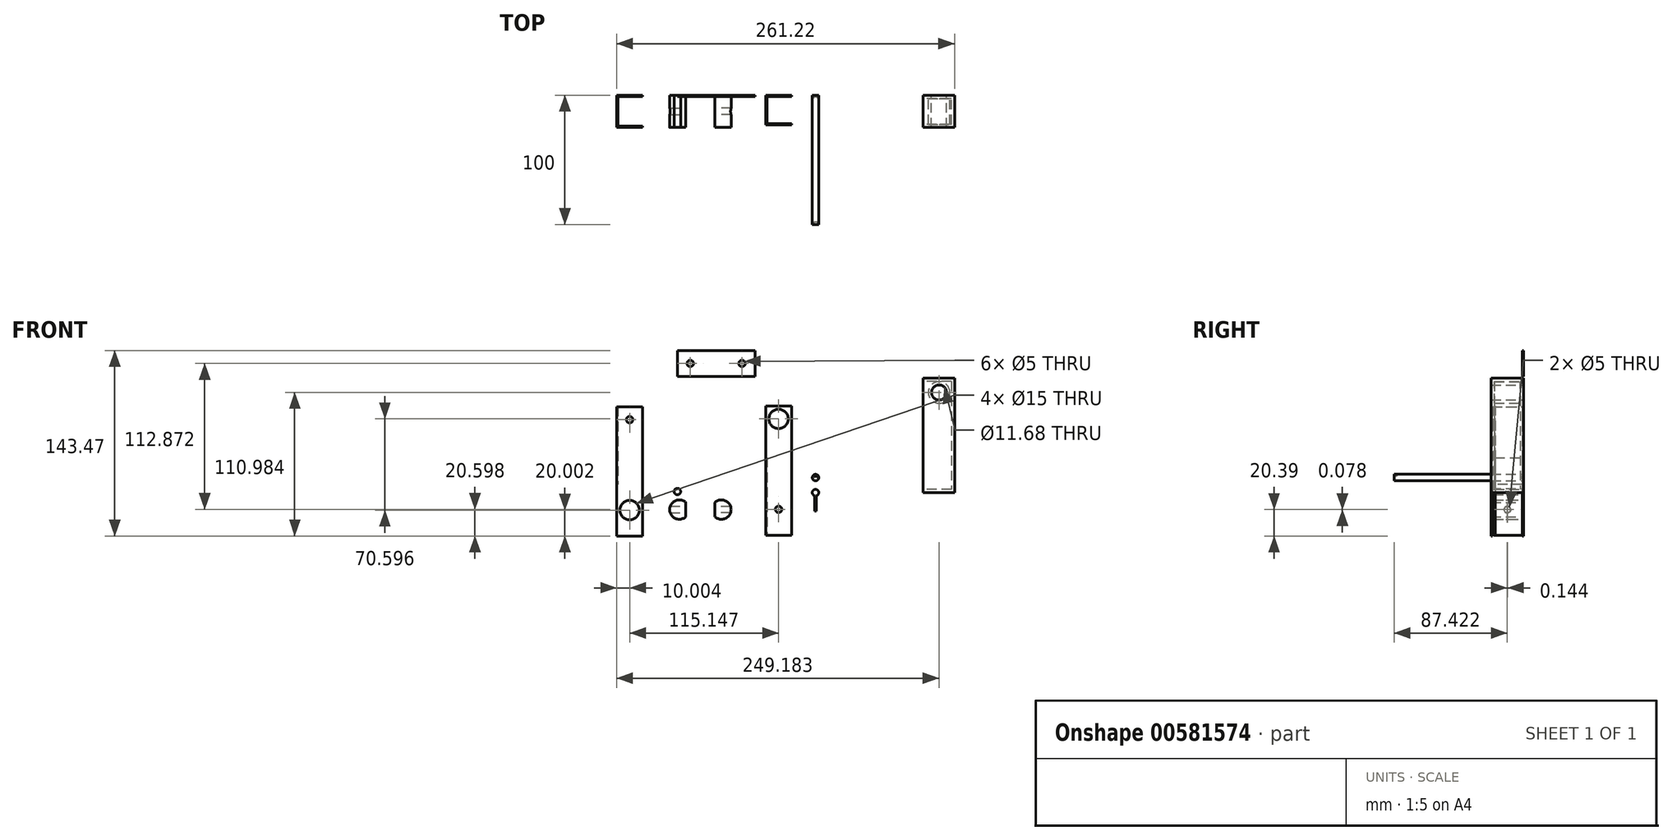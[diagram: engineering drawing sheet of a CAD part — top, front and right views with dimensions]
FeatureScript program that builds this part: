
annotation { "Feature Type Name" : "Feature", "Feature Type Description" : "" }
export const myFeature = defineFeature(function(context is Context, id is Id, definition is map)
    precondition{}
    {
        {
            var Q0;
            Q0=qCreatedBy(makeId("Front.planeOp"),FACE);
            var sketch = newSketch(context, id + "F0", { "sketchPlane" : qUnion([Q0])});
            skLineSegment(sketch, "E0.bottom", {"start": v(-95.37, 30.82) * mm, "end": v(-75.37, 30.82) * mm});
            skLineSegment(sketch, "E0.top", {"start": v(-95.37, -69.18) * mm, "end": v(-75.37, -69.18) * mm});
            skLineSegment(sketch, "E0.left", {"start": v(-95.37, 30.82) * mm, "end": v(-95.37, -69.18) * mm});
            skLineSegment(sketch, "E0.right", {"start": v(-75.37, 30.82) * mm, "end": v(-75.37, -69.18) * mm});
            skCircle(sketch, "E1", {"center": v(-85.37, 20.82) * mm, "radius": 2.5 * mm});
            skCircle(sketch, "E2", {"center": v(-85.37, -49.18) * mm, "radius": 7.5 * mm});
            skPoint(sketch, "E3.start.orphan", {"position": v(-85.37, 30.82) * mm});
            skCircle(sketch, "E4", {"center": v(-48.44, -34.8) * mm, "radius": 2.5 * mm});
            skArc(sketch, "E5", {"start": v(-41.92, -43.12) * mm, "mid": v(-54.42, -48.71) * mm, "end": v(-41.92, -54.3) * mm});
            skPoint(sketch, "E6.orphan", {"position": v(-95.37, 10.82) * mm});
            skPoint(sketch, "E7.start.orphan", {"position": v(-95.37, 20.82) * mm});
            skPoint(sketch, "E8.trimOffspring.end.orphan", {"position": v(-75.37, 20.82) * mm});
            skPoint(sketch, "E9.MirrorCS.end.orphan", {"position": v(-75.37, 10.82) * mm});
            skPoint(sketch, "E10.orphan", {"position": v(-95.37, 0.82) * mm});
            skPoint(sketch, "E11.MirrorCS.end.orphan", {"position": v(-75.37, 0.82) * mm});
            skPoint(sketch, "E12.orphan", {"position": v(-95.37, -19.18) * mm});
            skPoint(sketch, "E13.MirrorCS.end.orphan", {"position": v(-75.37, -19.18) * mm});
            skPoint(sketch, "E14.orphan", {"position": v(-95.37, -29.18) * mm});
            skPoint(sketch, "E15.MirrorCS.end.orphan", {"position": v(-75.37, -29.18) * mm});
            skPoint(sketch, "E16.orphan", {"position": v(-95.37, -59.18) * mm});
            skPoint(sketch, "E17.MirrorCS.end.orphan", {"position": v(-75.37, -59.18) * mm});
            skPoint(sketch, "E18.trimOffspring.end.orphan", {"position": v(-85.37, -69.18) * mm});
            skPoint(sketch, "E19.MirrorCS.start.orphan", {"position": v(-95.37, -49.18) * mm});
            skPoint(sketch, "E20.trimOffspring.end.orphan", {"position": v(-75.37, -49.18) * mm});
            skLineSegment(sketch, "E21.bottom", {"start": v(19.78, 31.42) * mm, "end": v(39.78, 31.42) * mm});
            skLineSegment(sketch, "E21.top", {"start": v(19.78, -68.58) * mm, "end": v(39.78, -68.58) * mm});
            skLineSegment(sketch, "E21.left", {"start": v(19.78, 31.42) * mm, "end": v(19.78, -68.58) * mm});
            skLineSegment(sketch, "E21.right", {"start": v(39.78, 31.42) * mm, "end": v(39.78, -68.58) * mm});
            skCircle(sketch, "E22", {"center": v(29.78, 21.42) * mm, "radius": 7.5 * mm});
            skCircle(sketch, "E23", {"center": v(29.78, -48.58) * mm, "radius": 2.5 * mm});
            skPoint(sketch, "E24.start.orphan", {"position": v(29.78, 31.42) * mm});
            skPoint(sketch, "E25.orphan", {"position": v(19.78, 11.42) * mm});
            skPoint(sketch, "E26.start.orphan", {"position": v(19.78, 21.42) * mm});
            skPoint(sketch, "E27.trimOffspring.end.orphan", {"position": v(39.78, 21.42) * mm});
            skPoint(sketch, "E28.MirrorCS.end.orphan", {"position": v(39.78, 11.42) * mm});
            skPoint(sketch, "E29.orphan", {"position": v(19.78, 1.42) * mm});
            skPoint(sketch, "E30.MirrorCS.end.orphan", {"position": v(39.78, 1.42) * mm});
            skPoint(sketch, "E31.orphan", {"position": v(19.78, -18.58) * mm});
            skPoint(sketch, "E32.MirrorCS.end.orphan", {"position": v(39.78, -18.58) * mm});
            skPoint(sketch, "E33.orphan", {"position": v(19.78, -28.58) * mm});
            skPoint(sketch, "E34.MirrorCS.end.orphan", {"position": v(39.78, -28.58) * mm});
            skPoint(sketch, "E35.orphan", {"position": v(19.78, -58.58) * mm});
            skPoint(sketch, "E36.MirrorCS.end.orphan", {"position": v(39.78, -58.58) * mm});
            skPoint(sketch, "E37.trimOffspring.end.orphan", {"position": v(29.78, -68.58) * mm});
            skPoint(sketch, "E38.MirrorCS.start.orphan", {"position": v(19.78, -48.58) * mm});
            skPoint(sketch, "E39.trimOffspring.end.orphan", {"position": v(39.78, -48.58) * mm});
            skLineSegment(sketch, "E40", {"start": v(-46.92, -41.21) * mm, "end": v(-46.92, -56.21) * mm, "construction": true});
            skLineSegment(sketch, "E41", {"start": v(-41.92, -43.12) * mm, "end": v(-41.92, -54.3) * mm});
            skLineSegment(sketch, "E42", {"start": v(-30.67, -23.09) * mm, "end": v(-30.67, -63.08) * mm, "construction": true});
            skLineSegment(sketch, "E43.MirrorCS", {"start": v(-19.42, -43.12) * mm, "end": v(-19.42, -54.3) * mm});
            skArc(sketch, "E44.MirrorCS", {"start": v(-19.42, -43.12) * mm, "mid": v(-6.92, -48.71) * mm, "end": v(-19.42, -54.3) * mm});
            skCircle(sketch, "E45", {"center": v(58.34, -24) * mm, "radius": 2.5 * mm});
            skArc(sketch, "E46", {"start": v(59.05, -38.03) * mm, "mid": v(58.34, -33.13) * mm, "end": v(57.64, -38.03) * mm});
            skLineSegment(sketch, "E47", {"start": v(59.05, -38.03) * mm, "end": v(59.05, -49.9) * mm});
            skLineSegment(sketch, "E48", {"start": v(59.05, -49.9) * mm, "end": v(58.34, -49.9) * mm});
            skLineSegment(sketch, "E49.MirrorCS", {"start": v(57.64, -38.03) * mm, "end": v(57.64, -49.9) * mm});
            skLineSegment(sketch, "E50.MirrorCS", {"start": v(57.64, -49.9) * mm, "end": v(58.34, -49.9) * mm});
            skLineSegment(sketch, "E51.bottom", {"start": v(11.5, 74.3) * mm, "end": v(-48.5, 74.3) * mm});
            skLineSegment(sketch, "E51.top", {"start": v(11.5, 54.3) * mm, "end": v(-48.5, 54.3) * mm});
            skLineSegment(sketch, "E51.left", {"start": v(11.5, 74.3) * mm, "end": v(11.5, 54.3) * mm});
            skLineSegment(sketch, "E51.right", {"start": v(-48.5, 74.3) * mm, "end": v(-48.5, 54.3) * mm});
            skCircle(sketch, "E52", {"center": v(1.5, 64.3) * mm, "radius": 2.5 * mm});
            skCircle(sketch, "E53", {"center": v(-38.5, 64.3) * mm, "radius": 2.5 * mm});
            skPoint(sketch, "E54.orphan", {"position": v(1.5, 74.3) * mm});
            skPoint(sketch, "E55.orphan", {"position": v(1.5, 54.3) * mm});
            skPoint(sketch, "E56.orphan", {"position": v(11.5, 64.3) * mm});
            skPoint(sketch, "E57.orphan", {"position": v(-48.5, 64.3) * mm});
            skPoint(sketch, "E58.orphan", {"position": v(-38.5, 74.3) * mm});
            skPoint(sketch, "E59.end.orphan", {"position": v(-38.5, 54.3) * mm});
            skLineSegment(sketch, "E60.bottom", {"start": v(165.85, 52.83) * mm, "end": v(141.44, 52.83) * mm});
            skLineSegment(sketch, "E60.top", {"start": v(165.85, -35.75) * mm, "end": v(141.44, -35.75) * mm});
            skLineSegment(sketch, "E60.left", {"start": v(165.85, 52.83) * mm, "end": v(165.85, -35.75) * mm});
            skLineSegment(sketch, "E60.right", {"start": v(141.44, 52.83) * mm, "end": v(141.44, -35.75) * mm});
            skCircle(sketch, "E61", {"center": v(153.81, 41.8) * mm, "radius": 5.84 * mm});
            skSolve(sketch);
        }
        {
            var Q0;
            Q0=makeQuery(id+"F0.imprint","IMPRINT",FACE,{"disambiguationData":[TD([[makeQuery(id+"F0.imprint","IMPRINT",EDGE,{"derivedFrom":sQuery(id+"F0.wireOp",EDGE,"E0.bottom")}),-1.0]])]});
            extrude(context, id + "F1", {"entities" : qUnion([Q0]), "depth" : 25 * mm, "offsetDistance" : 25 * mm});
        }
        {
            var Q0;
            Q0=makeQuery(id+"F0.imprint","IMPRINT",FACE,{"disambiguationData":[TD([[makeQuery(id+"F0.imprint","IMPRINT",EDGE,{"derivedFrom":sQuery(id+"F0.wireOp",EDGE,"E4")}),1.0]])]});
            extrude(context, id + "F2", {"entities" : qUnion([Q0]), "depth" : 25 * mm, "offsetDistance" : 25 * mm});
        }
        {
            var Q0;
            Q0=makeQuery(id+"F1.opExtrude","SWEPT_FACE",FACE,{"disambiguationData":[OSD([sQuery(id+"F0.wireOp",EDGE,"E0.top")])]});
            var sketch = newSketch(context, id + "F3", { "sketchPlane" : qUnion([Q0])});
            skLineSegment(sketch, "E62", {"start": v(-75.37, 24) * mm, "end": v(-94.37, 24) * mm});
            skLineSegment(sketch, "E63", {"start": v(-94.37, 24) * mm, "end": v(-94.37, 1) * mm});
            skLineSegment(sketch, "E64", {"start": v(-94.37, 1) * mm, "end": v(-75.37, 1) * mm});
            skSolve(sketch);
        }
        {
            var Q0;
            {var subQ0=sQuery(id+"F3.wireOp",EDGE,"E62");Q0=makeQuery(id+"F3.imprint","IMPRINT",FACE,{"disambiguationData":[TD([[makeQuery(id+"F3.imprint","IMPRINT",EDGE,{"derivedFrom":subQ0}),1.0]])]});}
            extrude(context, id + "F4", {"entities" : qUnion([Q0]), "operationType" : NewBodyOperationType.REMOVE, "oppositeDirection" : true, "depth" : 100 * mm, "offsetDistance" : 25 * mm});
        }
        {
            var Q0;
            Q0=makeQuery(id+"F0.imprint","IMPRINT",FACE,{"disambiguationData":[TD([[makeQuery(id+"F0.imprint","IMPRINT",EDGE,{"derivedFrom":sQuery(id+"F0.wireOp",EDGE,"E21.bottom")}),-1.0]])]});
            extrude(context, id + "F5", {"entities" : qUnion([Q0]), "depth" : 23 * mm, "offsetDistance" : 25 * mm});
        }
        {
            var Q0;
            Q0=makeQuery(id+"F5.opExtrude","SWEPT_FACE",FACE,{"disambiguationData":[OSD([sQuery(id+"F0.wireOp",EDGE,"E21.top")])]});
            var sketch = newSketch(context, id + "F6", { "sketchPlane" : qUnion([Q0])});
            skLineSegment(sketch, "E65", {"start": v(39.78, 22) * mm, "end": v(20.78, 22) * mm});
            skLineSegment(sketch, "E66", {"start": v(20.78, 22) * mm, "end": v(20.78, 1) * mm});
            skLineSegment(sketch, "E67", {"start": v(20.78, 1) * mm, "end": v(39.78, 1) * mm});
            skSolve(sketch);
        }
        {
            var Q0;
            {var subQ0=sQuery(id+"F6.wireOp",EDGE,"E65");Q0=makeQuery(id+"F6.imprint","IMPRINT",FACE,{"disambiguationData":[TD([[makeQuery(id+"F6.imprint","IMPRINT",EDGE,{"derivedFrom":subQ0}),1.0]])]});}
            extrude(context, id + "F7", {"entities" : qUnion([Q0]), "operationType" : NewBodyOperationType.REMOVE, "oppositeDirection" : true, "depth" : 100 * mm, "offsetDistance" : 25 * mm});
        }
        {
            var Q0;
            Q0=makeQuery(id+"F1.opExtrude","SWEPT_FACE",FACE,{"disambiguationData":[OSD([sQuery(id+"F0.wireOp",EDGE,"E0.left")])]});
            var sketch = newSketch(context, id + "F8", { "sketchPlane" : qUnion([Q0])});
            skLineSegment(sketch, "E68", {"start": v(1, -29.18) * mm, "end": v(1, -69.18) * mm});
            skLineSegment(sketch, "E69", {"start": v(1, -29.18) * mm, "end": v(24, -29.18) * mm});
            skLineSegment(sketch, "E70", {"start": v(24, -29.18) * mm, "end": v(24, -69.18) * mm});
            skLineSegment(sketch, "E71", {"start": v(0, -69.18) * mm, "end": v(0, -35.46) * mm});
            skLineSegment(sketch, "E72", {"start": v(25, -35.46) * mm, "end": v(25, -69.18) * mm});
            skSolve(sketch);
        }
        {
            var Q0;
            {var subQ0=sQuery(id+"F8.wireOp",EDGE,"E68");Q0=makeQuery(id+"F8.imprint","IMPRINT",FACE,{"disambiguationData":[TD([[makeQuery(id+"F8.imprint","IMPRINT",EDGE,{"derivedFrom":subQ0}),1.0]])]});}
            extrude(context, id + "F9", {"entities" : qUnion([Q0]), "operationType" : NewBodyOperationType.REMOVE, "endBound" : BoundingType.UP_TO_NEXT, "oppositeDirection" : true, "depth" : 25 * mm, "offsetDistance" : 25 * mm});
        }
        {
            var Q0;
            Q0=makeQuery(id+"F5.opExtrude","SWEPT_FACE",FACE,{"disambiguationData":[OSD([sQuery(id+"F0.wireOp",EDGE,"E21.left")])]});
            var sketch = newSketch(context, id + "F10", { "sketchPlane" : qUnion([Q0])});
            skLineSegment(sketch, "E73", {"start": v(1, 31.42) * mm, "end": v(1, -8.58) * mm});
            skLineSegment(sketch, "E74", {"start": v(1, -8.58) * mm, "end": v(22, -8.58) * mm});
            skLineSegment(sketch, "E75", {"start": v(22, -8.58) * mm, "end": v(22, 31.42) * mm});
            skSolve(sketch);
        }
        {
            var Q0;
            {var subQ0=sQuery(id+"F10.wireOp",EDGE,"E73");Q0=makeQuery(id+"F10.imprint","IMPRINT",FACE,{"disambiguationData":[TD([[makeQuery(id+"F10.imprint","IMPRINT",EDGE,{"derivedFrom":subQ0}),1.0]])]});}
            extrude(context, id + "F11", {"entities" : qUnion([Q0]), "operationType" : NewBodyOperationType.REMOVE, "endBound" : BoundingType.UP_TO_NEXT, "oppositeDirection" : true, "depth" : 25 * mm, "offsetDistance" : 25 * mm});
        }
        {
            var Q0;
            Q0=makeQuery(id+"F0.imprint","IMPRINT",FACE,{"disambiguationData":[TD([[makeQuery(id+"F0.imprint","IMPRINT",EDGE,{"derivedFrom":sQuery(id+"F0.wireOp",EDGE,"E5")}),1.0]])]});
            extrude(context, id + "F12", {"entities" : qUnion([Q0]), "depth" : 25 * mm, "offsetDistance" : 25 * mm});
        }
        {
            var Q0;
            Q0=makeQuery(id+"F12.opExtrude","SWEPT_FACE",FACE,{"disambiguationData":[OSD([sQuery(id+"F0.wireOp",EDGE,"E41")])]});
            var sketch = newSketch(context, id + "F13", { "sketchPlane" : qUnion([Q0])});
            skCircle(sketch, "E76", {"center": v(-12.43, -48.71) * mm, "radius": 2.5 * mm});
            skPoint(sketch, "E76.centerSnap0", {"position": v(-25, -48.71) * mm});
            skSolve(sketch);
        }
        {
            var Q0;
            Q0=makeQuery(id+"F13.imprint","IMPRINT",FACE,{"disambiguationData":[TD([[makeQuery(id+"F13.imprint","IMPRINT",EDGE,{"derivedFrom":sQuery(id+"F13.wireOp",EDGE,"E76")}),1.0]])]});
            extrude(context, id + "F14", {"entities" : qUnion([Q0]), "operationType" : NewBodyOperationType.REMOVE, "endBound" : BoundingType.UP_TO_NEXT, "oppositeDirection" : true, "depth" : 25 * mm, "offsetDistance" : 25 * mm});
        }
        {
            var Q0;
            Q0=makeQuery(id+"F0.imprint","IMPRINT",FACE,{"disambiguationData":[TD([[makeQuery(id+"F0.imprint","IMPRINT",EDGE,{"derivedFrom":sQuery(id+"F0.wireOp",EDGE,"E43.MirrorCS")}),1.0]])]});
            extrude(context, id + "F15", {"entities" : qUnion([Q0]), "depth" : 25 * mm, "offsetDistance" : 25 * mm});
        }
        {
            var Q0;
            Q0=makeQuery(id+"F15.opExtrude","SWEPT_FACE",FACE,{"disambiguationData":[OSD([sQuery(id+"F0.wireOp",EDGE,"E43.MirrorCS")])]});
            var sketch = newSketch(context, id + "F16", { "sketchPlane" : qUnion([Q0])});
            skCircle(sketch, "E77", {"center": v(12.58, -48.79) * mm, "radius": 2.5 * mm});
            skSolve(sketch);
        }
        {
            var Q0;
            Q0=makeQuery(id+"F16.imprint","IMPRINT",FACE,{"disambiguationData":[TD([[makeQuery(id+"F16.imprint","IMPRINT",EDGE,{"derivedFrom":sQuery(id+"F16.wireOp",EDGE,"E77")}),1.0]])]});
            extrude(context, id + "F17", {"entities" : qUnion([Q0]), "operationType" : NewBodyOperationType.REMOVE, "endBound" : BoundingType.UP_TO_NEXT, "oppositeDirection" : true, "depth" : 25 * mm, "offsetDistance" : 25 * mm});
        }
        {
            var Q0;
            Q0=makeQuery(id+"F0.imprint","IMPRINT",FACE,{"disambiguationData":[TD([[makeQuery(id+"F0.imprint","IMPRINT",EDGE,{"derivedFrom":sQuery(id+"F0.wireOp",EDGE,"E45")}),1.0]])]});
            extrude(context, id + "F18", {"entities" : qUnion([Q0]), "depth" : 100 * mm, "offsetDistance" : 25 * mm});
        }
        {
            var Q0;
            Q0=makeQuery(id+"F0.imprint","IMPRINT",FACE,{"disambiguationData":[TD([[makeQuery(id+"F0.imprint","IMPRINT",EDGE,{"derivedFrom":sQuery(id+"F0.wireOp",EDGE,"E46")}),1.0]])]});
            extrude(context, id + "F19", {"entities" : qUnion([Q0]), "depth" : 1 * mm, "offsetDistance" : 25 * mm});
        }
        {
            var Q0;
            Q0=makeQuery(id+"F18.opExtrude","CAP_FACE",FACE,{"disambiguationData":[OSD([sQuery(id+"F0.wireOp",EDGE,"E45")])],"isStart":false});
            var sketch = newSketch(context, id + "F20", { "sketchPlane" : qUnion([Q0])});
            skLineSegment(sketch, "E78.bottom", {"start": v(57.45, -22.57) * mm, "end": v(59.44, -22.57) * mm});
            skLineSegment(sketch, "E78.top", {"start": v(57.45, -22.97) * mm, "end": v(59.44, -22.97) * mm});
            skLineSegment(sketch, "E78.left", {"start": v(57.45, -22.57) * mm, "end": v(57.45, -22.97) * mm});
            skLineSegment(sketch, "E78.right", {"start": v(59.44, -22.57) * mm, "end": v(59.44, -22.97) * mm});
            skSolve(sketch);
        }
        {
            var Q0;
            Q0=makeQuery(id+"F20.imprint","IMPRINT",FACE,{"disambiguationData":[TD([[makeQuery(id+"F20.imprint","IMPRINT",EDGE,{"derivedFrom":sQuery(id+"F20.wireOp",EDGE,"E78.bottom")}),-1.0]])]});
            extrude(context, id + "F21", {"entities" : qUnion([Q0]), "operationType" : NewBodyOperationType.REMOVE, "oppositeDirection" : true, "depth" : 2 * mm, "offsetDistance" : 25 * mm});
        }
        {
            var Q0;
            Q0=makeQuery(id+"F0.imprint","IMPRINT",FACE,{"disambiguationData":[TD([[makeQuery(id+"F0.imprint","IMPRINT",EDGE,{"derivedFrom":sQuery(id+"F0.wireOp",EDGE,"E45")}),1.0]])]});
            var sketch = newSketch(context, id + "F22", { "sketchPlane" : qUnion([Q0])});
            skLineSegment(sketch, "E79.bottom", {"start": v(60.03, -23.09) * mm, "end": v(59.56, -23.09) * mm});
            skLineSegment(sketch, "E79.top", {"start": v(60.03, -24.5) * mm, "end": v(59.56, -24.5) * mm});
            skLineSegment(sketch, "E79.left", {"start": v(60.03, -23.09) * mm, "end": v(60.03, -24.5) * mm});
            skLineSegment(sketch, "E79.right", {"start": v(59.56, -23.09) * mm, "end": v(59.56, -24.5) * mm});
            skLineSegment(sketch, "E80.bottom", {"start": v(57.29, -23.04) * mm, "end": v(56.87, -23.04) * mm});
            skLineSegment(sketch, "E80.top", {"start": v(57.29, -24.06) * mm, "end": v(56.87, -24.06) * mm});
            skLineSegment(sketch, "E80.left", {"start": v(57.29, -23.04) * mm, "end": v(57.29, -24.06) * mm});
            skLineSegment(sketch, "E80.right", {"start": v(56.87, -23.04) * mm, "end": v(56.87, -24.06) * mm});
            skSolve(sketch);
        }
        {
            var Q0;
            Q0=makeQuery(id+"F22.imprint","IMPRINT",FACE,{"disambiguationData":[TD([[makeQuery(id+"F22.imprint","IMPRINT",EDGE,{"derivedFrom":sQuery(id+"F22.wireOp",EDGE,"E79.bottom")}),1.0]])]});
            var Q1;
            Q1=makeQuery(id+"F22.imprint","IMPRINT",FACE,{"disambiguationData":[TD([[makeQuery(id+"F22.imprint","IMPRINT",EDGE,{"derivedFrom":sQuery(id+"F22.wireOp",EDGE,"E80.bottom")}),1.0]])]});
            extrude(context, id + "F23", {"entities" : qUnion([Q0, Q1]), "operationType" : NewBodyOperationType.REMOVE, "depth" : 2 * mm, "offsetDistance" : 25 * mm});
        }
        {
            var Q0;
            Q0=makeQuery(id+"F0.imprint","IMPRINT",FACE,{"disambiguationData":[TD([[makeQuery(id+"F0.imprint","IMPRINT",EDGE,{"derivedFrom":sQuery(id+"F0.wireOp",EDGE,"E51.bottom")}),1.0]])]});
            extrude(context, id + "F24", {"entities" : qUnion([Q0]), "depth" : 1 * mm, "offsetDistance" : 25 * mm});
        }
        {
            var Q0;
            Q0=makeQuery(id+"F0.imprint","IMPRINT",FACE,{"disambiguationData":[TD([[makeQuery(id+"F0.imprint","IMPRINT",EDGE,{"derivedFrom":sQuery(id+"F0.wireOp",EDGE,"E60.bottom")}),1.0]])]});
            extrude(context, id + "F25", {"entities" : qUnion([Q0]), "depth" : 25 * mm, "offsetDistance" : 25 * mm});
        }
        {
            var Q0;
            Q0=makeQuery(id+"F25.opExtrude","SWEPT_FACE",FACE,{"disambiguationData":[OSD([sQuery(id+"F0.wireOp",EDGE,"E60.right")])]});
            shell(context, id + "F26", {"entities" : qUnion([Q0]), "thickness" : 2.5 * mm});
        }
    });
